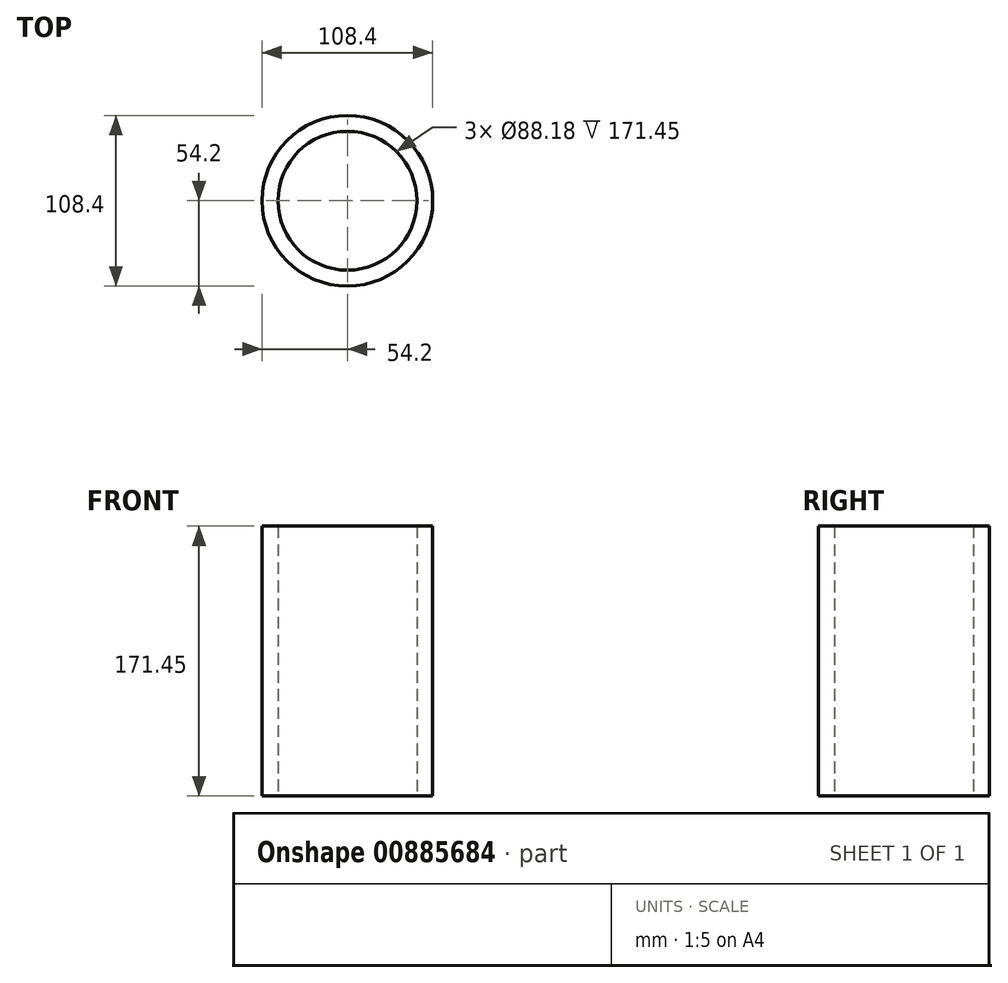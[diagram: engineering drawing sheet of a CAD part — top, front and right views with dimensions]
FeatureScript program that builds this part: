
annotation { "Feature Type Name" : "Feature", "Feature Type Description" : "" }
export const myFeature = defineFeature(function(context is Context, id is Id, definition is map)
    precondition{}
    {
        {
            var Q0;
            Q0=qCreatedBy(makeId("Top.planeOp"),FACE);
            var sketch = newSketch(context, id + "F0", { "sketchPlane" : qUnion([Q0])});
            skCircle(sketch, "E0", {"center": v(0, 0) * mm, "radius": 54.2 * mm});
            skCircle(sketch, "E1", {"center": v(0, 0) * mm, "radius": 44.1 * mm});
            skSolve(sketch);
        }
        {
            var Q0;
            Q0=makeQuery(id+"F0.imprint","IMPRINT",FACE,{"disambiguationData":[TD([[makeQuery(id+"F0.imprint","IMPRINT",EDGE,{"derivedFrom":sQuery(id+"F0.wireOp",EDGE,"E0")}),1.0]])]});
            extrude(context, id + "F1", {"entities" : qUnion([Q0]), "depth" : 171.45 * mm, "offsetDistance" : 25.4 * mm});
        }
    });
